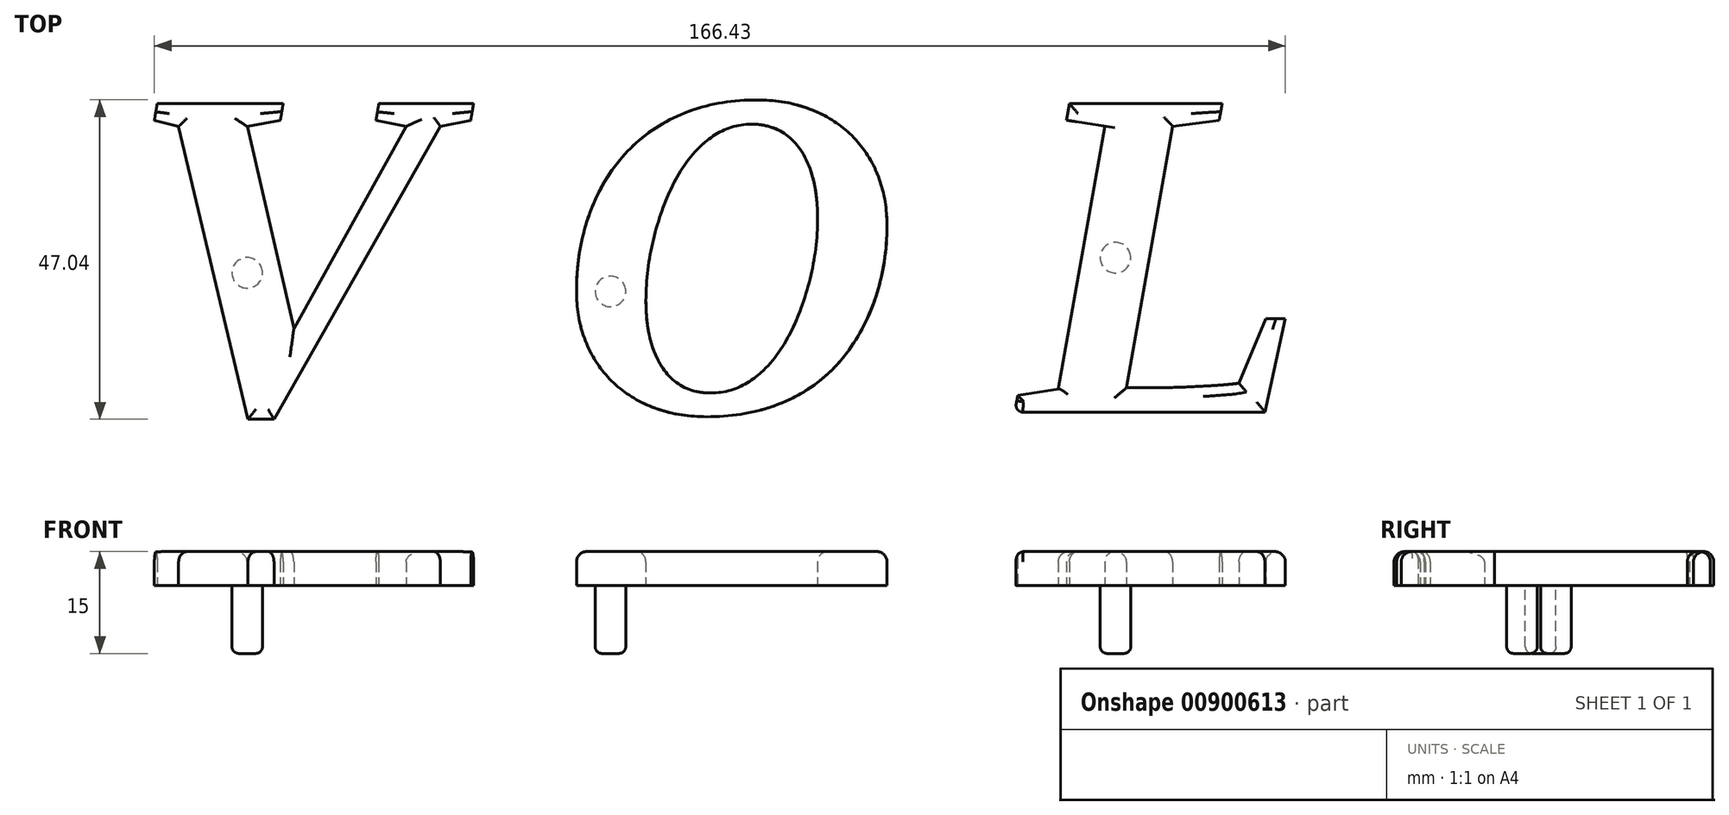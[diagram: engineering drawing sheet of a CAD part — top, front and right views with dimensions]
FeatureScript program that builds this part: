
annotation { "Feature Type Name" : "Feature", "Feature Type Description" : "" }
export const myFeature = defineFeature(function(context is Context, id is Id, definition is map)
    precondition{}
    {
        {
            var Q0;
            Q0=qCreatedBy(makeId("Top.planeOp"),FACE);
            var sketch = newSketch(context, id + "F0", { "sketchPlane" : qUnion([Q0])});
            skText(sketch, "E0", { "text": "V O L V O\n", "fontName": "Tinos-BoldItalic.ttf"});
            skPoint(sketch, "E1", {"position": v(51.81, -31.4) * mm});
            skPoint(sketch, "E2", {"position": v(27.28, -4.45) * mm});
            const initialGuessF0  = {"E0": [-0.05026, -0.04222, 1, 0, 0.05]};
            skSetInitialGuess(sketch, initialGuessF0);
            skSolve(sketch);
        }
        {
            var Q0;
            Q0 = qSketchRegion(id + "F0", true);
            extrude(context, id + "F1", {"entities" : qUnion([Q0]), "depth" : 5 * mm, "offsetDistance" : 25.4 * mm});
        }
        {
            var Q0;
            Q0=makeQuery(id+"F1.opExtrude","CAP_FACE",FACE,{"disambiguationData":[OSD([sQuery(id+"F0.wireOp",EDGE,"E0.sketch_text.stroke-0"),sQuery(id+"F0.wireOp",EDGE,"E0.sketch_text.stroke-1"),sQuery(id+"F0.wireOp",EDGE,"E0.sketch_text.stroke-2"),sQuery(id+"F0.wireOp",EDGE,"E0.sketch_text.stroke-3"),sQuery(id+"F0.wireOp",EDGE,"E0.sketch_text.stroke-4"),sQuery(id+"F0.wireOp",EDGE,"E0.sketch_text.stroke-5"),sQuery(id+"F0.wireOp",EDGE,"E0.sketch_text.stroke-6"),sQuery(id+"F0.wireOp",EDGE,"E0.sketch_text.stroke-7"),sQuery(id+"F0.wireOp",EDGE,"E0.sketch_text.stroke-8"),sQuery(id+"F0.wireOp",EDGE,"E0.sketch_text.stroke-9"),sQuery(id+"F0.wireOp",EDGE,"E0.sketch_text.stroke-10"),sQuery(id+"F0.wireOp",EDGE,"E0.sketch_text.stroke-11"),sQuery(id+"F0.wireOp",EDGE,"E0.sketch_text.stroke-12"),sQuery(id+"F0.wireOp",EDGE,"E0.sketch_text.stroke-13"),sQuery(id+"F0.wireOp",EDGE,"E0.sketch_text.stroke-14")])],"isStart":true});
            var sketch = newSketch(context, id + "F2", { "sketchPlane" : qUnion([Q0])});
            skPoint(sketch, "E3", {"position": v(-32.53, 21.7) * mm});
            skPoint(sketch, "E3.positionSnap0", {"position": v(-37.53, 21.7) * mm});
            skCircle(sketch, "E4", {"center": v(-32.53, 21.7) * mm, "radius": 2.25 * mm});
            skSolve(sketch);
        }
        {
            var Q0;
            Q0 = qSketchRegion(id + "F2", true);
            extrude(context, id + "F3", {"entities" : qUnion([Q0]), "operationType" : NewBodyOperationType.ADD, "depth" : 10 * mm, "offsetDistance" : 25 * mm});
        }
        {
            var Q0;
            Q0=makeQuery(id+"F1.opExtrude","CAP_FACE",FACE,{"disambiguationData":[OSD([sQuery(id+"F0.wireOp",EDGE,"E0.sketch_text.stroke-15"),sQuery(id+"F0.wireOp",EDGE,"E0.sketch_text.stroke-16"),sQuery(id+"F0.wireOp",EDGE,"E0.sketch_text.stroke-17"),sQuery(id+"F0.wireOp",EDGE,"E0.sketch_text.stroke-18"),sQuery(id+"F0.wireOp",EDGE,"E0.sketch_text.stroke-19"),sQuery(id+"F0.wireOp",EDGE,"E0.sketch_text.stroke-20"),sQuery(id+"F0.wireOp",EDGE,"E0.sketch_text.stroke-21"),sQuery(id+"F0.wireOp",EDGE,"E0.sketch_text.stroke-22"),sQuery(id+"F0.wireOp",EDGE,"E0.sketch_text.stroke-23"),sQuery(id+"F0.wireOp",EDGE,"E0.sketch_text.stroke-24"),sQuery(id+"F0.wireOp",EDGE,"E0.sketch_text.stroke-25"),sQuery(id+"F0.wireOp",EDGE,"E0.sketch_text.stroke-26"),sQuery(id+"F0.wireOp",EDGE,"E0.sketch_text.stroke-27"),sQuery(id+"F0.wireOp",EDGE,"E0.sketch_text.stroke-28"),sQuery(id+"F0.wireOp",EDGE,"E0.sketch_text.stroke-29"),sQuery(id+"F0.wireOp",EDGE,"E0.sketch_text.stroke-30"),sQuery(id+"F0.wireOp",EDGE,"E0.sketch_text.stroke-31"),sQuery(id+"F0.wireOp",EDGE,"E0.sketch_text.stroke-32"),sQuery(id+"F0.wireOp",EDGE,"E0.sketch_text.stroke-33"),sQuery(id+"F0.wireOp",EDGE,"E0.sketch_text.stroke-34"),sQuery(id+"F0.wireOp",EDGE,"E0.sketch_text.stroke-35"),sQuery(id+"F0.wireOp",EDGE,"E0.sketch_text.stroke-36")])],"isStart":true});
            var sketch = newSketch(context, id + "F4", { "sketchPlane" : qUnion([Q0])});
            skPoint(sketch, "E5", {"position": v(20.93, 24.45) * mm});
            skCircle(sketch, "E6", {"center": v(20.93, 24.45) * mm, "radius": 2.25 * mm});
            skSolve(sketch);
        }
        {
            var Q0;
            Q0 = qSketchRegion(id + "F4", true);
            extrude(context, id + "F5", {"entities" : qUnion([Q0]), "operationType" : NewBodyOperationType.ADD, "depth" : 10 * mm, "offsetDistance" : 25 * mm});
        }
        {
            var Q0;
            Q0=makeQuery(id+"F1.opExtrude","CAP_FACE",FACE,{"disambiguationData":[OSD([sQuery(id+"F0.wireOp",EDGE,"E0.sketch_text.stroke-37"),sQuery(id+"F0.wireOp",EDGE,"E0.sketch_text.stroke-38"),sQuery(id+"F0.wireOp",EDGE,"E0.sketch_text.stroke-39"),sQuery(id+"F0.wireOp",EDGE,"E0.sketch_text.stroke-40"),sQuery(id+"F0.wireOp",EDGE,"E0.sketch_text.stroke-41"),sQuery(id+"F0.wireOp",EDGE,"E0.sketch_text.stroke-42"),sQuery(id+"F0.wireOp",EDGE,"E0.sketch_text.stroke-43"),sQuery(id+"F0.wireOp",EDGE,"E0.sketch_text.stroke-44"),sQuery(id+"F0.wireOp",EDGE,"E0.sketch_text.stroke-45"),sQuery(id+"F0.wireOp",EDGE,"E0.sketch_text.stroke-46"),sQuery(id+"F0.wireOp",EDGE,"E0.sketch_text.stroke-47"),sQuery(id+"F0.wireOp",EDGE,"E0.sketch_text.stroke-48"),sQuery(id+"F0.wireOp",EDGE,"E0.sketch_text.stroke-49"),sQuery(id+"F0.wireOp",EDGE,"E0.sketch_text.stroke-50"),sQuery(id+"F0.wireOp",EDGE,"E0.sketch_text.stroke-51"),sQuery(id+"F0.wireOp",EDGE,"E0.sketch_text.stroke-52")])],"isStart":true});
            var sketch = newSketch(context, id + "F6", { "sketchPlane" : qUnion([Q0])});
            skPoint(sketch, "E7", {"position": v(95.24, 19.47) * mm});
            skPoint(sketch, "E7.positionSnap0", {"position": v(90.24, 19.47) * mm});
            skCircle(sketch, "E8", {"center": v(95.24, 19.47) * mm, "radius": 2.25 * mm});
            skSolve(sketch);
        }
        {
            var Q0;
            Q0 = qSketchRegion(id + "F6", true);
            extrude(context, id + "F7", {"entities" : qUnion([Q0]), "operationType" : NewBodyOperationType.ADD, "depth" : 10 * mm, "offsetDistance" : 25 * mm});
        }
        {
            var Q0;
            Q0=makeQuery(id+"F1.opExtrude","SWEPT_BODY",BODY,{"disambiguationData":[OSD([sQuery(id+"F0.wireOp",EDGE,"E0.sketch_text.stroke-53"),sQuery(id+"F0.wireOp",EDGE,"E0.sketch_text.stroke-54"),sQuery(id+"F0.wireOp",EDGE,"E0.sketch_text.stroke-55"),sQuery(id+"F0.wireOp",EDGE,"E0.sketch_text.stroke-56"),sQuery(id+"F0.wireOp",EDGE,"E0.sketch_text.stroke-57"),sQuery(id+"F0.wireOp",EDGE,"E0.sketch_text.stroke-58"),sQuery(id+"F0.wireOp",EDGE,"E0.sketch_text.stroke-59"),sQuery(id+"F0.wireOp",EDGE,"E0.sketch_text.stroke-60"),sQuery(id+"F0.wireOp",EDGE,"E0.sketch_text.stroke-61"),sQuery(id+"F0.wireOp",EDGE,"E0.sketch_text.stroke-62"),sQuery(id+"F0.wireOp",EDGE,"E0.sketch_text.stroke-63"),sQuery(id+"F0.wireOp",EDGE,"E0.sketch_text.stroke-64"),sQuery(id+"F0.wireOp",EDGE,"E0.sketch_text.stroke-65"),sQuery(id+"F0.wireOp",EDGE,"E0.sketch_text.stroke-66"),sQuery(id+"F0.wireOp",EDGE,"E0.sketch_text.stroke-67")])]});
            var Q1;
            Q1=makeQuery(id+"F1.opExtrude","SWEPT_BODY",BODY,{"disambiguationData":[OSD([sQuery(id+"F0.wireOp",EDGE,"E0.sketch_text.stroke-68"),sQuery(id+"F0.wireOp",EDGE,"E0.sketch_text.stroke-69"),sQuery(id+"F0.wireOp",EDGE,"E0.sketch_text.stroke-70"),sQuery(id+"F0.wireOp",EDGE,"E0.sketch_text.stroke-71"),sQuery(id+"F0.wireOp",EDGE,"E0.sketch_text.stroke-72"),sQuery(id+"F0.wireOp",EDGE,"E0.sketch_text.stroke-73"),sQuery(id+"F0.wireOp",EDGE,"E0.sketch_text.stroke-74"),sQuery(id+"F0.wireOp",EDGE,"E0.sketch_text.stroke-75"),sQuery(id+"F0.wireOp",EDGE,"E0.sketch_text.stroke-76"),sQuery(id+"F0.wireOp",EDGE,"E0.sketch_text.stroke-77"),sQuery(id+"F0.wireOp",EDGE,"E0.sketch_text.stroke-78"),sQuery(id+"F0.wireOp",EDGE,"E0.sketch_text.stroke-79"),sQuery(id+"F0.wireOp",EDGE,"E0.sketch_text.stroke-80"),sQuery(id+"F0.wireOp",EDGE,"E0.sketch_text.stroke-81"),sQuery(id+"F0.wireOp",EDGE,"E0.sketch_text.stroke-82"),sQuery(id+"F0.wireOp",EDGE,"E0.sketch_text.stroke-83"),sQuery(id+"F0.wireOp",EDGE,"E0.sketch_text.stroke-84"),sQuery(id+"F0.wireOp",EDGE,"E0.sketch_text.stroke-85"),sQuery(id+"F0.wireOp",EDGE,"E0.sketch_text.stroke-86"),sQuery(id+"F0.wireOp",EDGE,"E0.sketch_text.stroke-87"),sQuery(id+"F0.wireOp",EDGE,"E0.sketch_text.stroke-88"),sQuery(id+"F0.wireOp",EDGE,"E0.sketch_text.stroke-89")])]});
            deleteBodies(context, id + "F8", {"entities" : qUnion([Q0, Q1])});
        }
        {
            var Q0;
            Q0=makeQuery(id+"F1.opExtrude","CAP_FACE",FACE,{"disambiguationData":[OSD([sQuery(id+"F0.wireOp",EDGE,"E0.sketch_text.stroke-0"),sQuery(id+"F0.wireOp",EDGE,"E0.sketch_text.stroke-1"),sQuery(id+"F0.wireOp",EDGE,"E0.sketch_text.stroke-2"),sQuery(id+"F0.wireOp",EDGE,"E0.sketch_text.stroke-3"),sQuery(id+"F0.wireOp",EDGE,"E0.sketch_text.stroke-4"),sQuery(id+"F0.wireOp",EDGE,"E0.sketch_text.stroke-5"),sQuery(id+"F0.wireOp",EDGE,"E0.sketch_text.stroke-6"),sQuery(id+"F0.wireOp",EDGE,"E0.sketch_text.stroke-7"),sQuery(id+"F0.wireOp",EDGE,"E0.sketch_text.stroke-8"),sQuery(id+"F0.wireOp",EDGE,"E0.sketch_text.stroke-9"),sQuery(id+"F0.wireOp",EDGE,"E0.sketch_text.stroke-10"),sQuery(id+"F0.wireOp",EDGE,"E0.sketch_text.stroke-11"),sQuery(id+"F0.wireOp",EDGE,"E0.sketch_text.stroke-12"),sQuery(id+"F0.wireOp",EDGE,"E0.sketch_text.stroke-13"),sQuery(id+"F0.wireOp",EDGE,"E0.sketch_text.stroke-14")])],"isStart":false});
            var Q1;
            Q1=makeQuery(id+"F1.opExtrude","CAP_FACE",FACE,{"disambiguationData":[OSD([sQuery(id+"F0.wireOp",EDGE,"E0.sketch_text.stroke-15"),sQuery(id+"F0.wireOp",EDGE,"E0.sketch_text.stroke-16"),sQuery(id+"F0.wireOp",EDGE,"E0.sketch_text.stroke-17"),sQuery(id+"F0.wireOp",EDGE,"E0.sketch_text.stroke-18"),sQuery(id+"F0.wireOp",EDGE,"E0.sketch_text.stroke-19"),sQuery(id+"F0.wireOp",EDGE,"E0.sketch_text.stroke-20"),sQuery(id+"F0.wireOp",EDGE,"E0.sketch_text.stroke-21"),sQuery(id+"F0.wireOp",EDGE,"E0.sketch_text.stroke-22"),sQuery(id+"F0.wireOp",EDGE,"E0.sketch_text.stroke-23"),sQuery(id+"F0.wireOp",EDGE,"E0.sketch_text.stroke-24"),sQuery(id+"F0.wireOp",EDGE,"E0.sketch_text.stroke-25"),sQuery(id+"F0.wireOp",EDGE,"E0.sketch_text.stroke-26"),sQuery(id+"F0.wireOp",EDGE,"E0.sketch_text.stroke-27"),sQuery(id+"F0.wireOp",EDGE,"E0.sketch_text.stroke-28"),sQuery(id+"F0.wireOp",EDGE,"E0.sketch_text.stroke-29"),sQuery(id+"F0.wireOp",EDGE,"E0.sketch_text.stroke-30"),sQuery(id+"F0.wireOp",EDGE,"E0.sketch_text.stroke-31"),sQuery(id+"F0.wireOp",EDGE,"E0.sketch_text.stroke-32"),sQuery(id+"F0.wireOp",EDGE,"E0.sketch_text.stroke-33"),sQuery(id+"F0.wireOp",EDGE,"E0.sketch_text.stroke-34"),sQuery(id+"F0.wireOp",EDGE,"E0.sketch_text.stroke-35"),sQuery(id+"F0.wireOp",EDGE,"E0.sketch_text.stroke-36")])],"isStart":false});
            var Q2;
            Q2=makeQuery(id+"F1.opExtrude","CAP_EDGE",EDGE,{"disambiguationData":[OSD([sQuery(id+"F0.wireOp",EDGE,"E0.sketch_text.stroke-49")])],"isStart":false});
            var Q3;
            Q3=makeQuery(id+"F1.opExtrude","CAP_EDGE",EDGE,{"disambiguationData":[OSD([sQuery(id+"F0.wireOp",EDGE,"E0.sketch_text.stroke-48")])],"isStart":false});
            var Q4;
            Q4=makeQuery(id+"F1.opExtrude","CAP_EDGE",EDGE,{"disambiguationData":[OSD([sQuery(id+"F0.wireOp",EDGE,"E0.sketch_text.stroke-46")])],"isStart":false});
            var Q5;
            Q5=makeQuery(id+"F1.opExtrude","CAP_EDGE",EDGE,{"disambiguationData":[OSD([sQuery(id+"F0.wireOp",EDGE,"E0.sketch_text.stroke-52")])],"isStart":false});
            var Q6;
            Q6=makeQuery(id+"F1.opExtrude","CAP_EDGE",EDGE,{"disambiguationData":[OSD([sQuery(id+"F0.wireOp",EDGE,"E0.sketch_text.stroke-51")])],"isStart":false});
            var Q7;
            Q7=makeQuery(id+"F1.opExtrude","CAP_EDGE",EDGE,{"disambiguationData":[OSD([sQuery(id+"F0.wireOp",EDGE,"E0.sketch_text.stroke-50")])],"isStart":false});
            var Q8;
            Q8=makeQuery(id+"F1.opExtrude","CAP_EDGE",EDGE,{"disambiguationData":[OSD([sQuery(id+"F0.wireOp",EDGE,"E0.sketch_text.stroke-37")])],"isStart":false});
            var Q9;
            Q9=makeQuery(id+"F1.opExtrude","CAP_EDGE",EDGE,{"disambiguationData":[OSD([sQuery(id+"F0.wireOp",EDGE,"E0.sketch_text.stroke-38")])],"isStart":false});
            var Q10;
            Q10=makeQuery(id+"F1.opExtrude","CAP_EDGE",EDGE,{"disambiguationData":[OSD([sQuery(id+"F0.wireOp",EDGE,"E0.sketch_text.stroke-40")])],"isStart":false});
            var Q11;
            Q11=makeQuery(id+"F1.opExtrude","CAP_EDGE",EDGE,{"disambiguationData":[OSD([sQuery(id+"F0.wireOp",EDGE,"E0.sketch_text.stroke-41")])],"isStart":false});
            var Q12;
            Q12=makeQuery(id+"F1.opExtrude","CAP_EDGE",EDGE,{"disambiguationData":[OSD([sQuery(id+"F0.wireOp",EDGE,"E0.sketch_text.stroke-42")])],"isStart":false});
            var Q13;
            Q13=makeQuery(id+"F1.opExtrude","CAP_EDGE",EDGE,{"disambiguationData":[OSD([sQuery(id+"F0.wireOp",EDGE,"E0.sketch_text.stroke-43")])],"isStart":false});
            fillet(context, id + "F9", {"entities" : qUnion([Q0, Q1, Q2, Q3, Q4, Q5, Q6, Q7, Q8, Q9, Q10, Q11, Q12, Q13]), "radius" : 1.5 * mm, "tangentPropagation" : true, "allowEdgeOverflow" : false});
        }
        {
            var Q0;
            Q0=makeQuery(id+"F1.opExtrude","CAP_EDGE",EDGE,{"disambiguationData":[OSD([sQuery(id+"F0.wireOp",EDGE,"E0.sketch_text.stroke-44")])],"isStart":false});
            var Q1;
            Q1=makeQuery(id+"F1.opExtrude","CAP_EDGE",EDGE,{"disambiguationData":[OSD([sQuery(id+"F0.wireOp",EDGE,"E0.sketch_text.stroke-45")])],"isStart":false});
            fillet(context, id + "F10", {"entities" : qUnion([Q0, Q1]), "radius" : 1 * mm, "tangentPropagation" : true, "allowEdgeOverflow" : false});
        }
        {
            var Q0;
            Q0=makeQuery(id+"F7.opExtrude","CAP_EDGE",EDGE,{"disambiguationData":[OSD([sQuery(id+"F6.wireOp",EDGE,"E8")])],"isStart":false});
            var Q1;
            Q1=makeQuery(id+"F5.opExtrude","CAP_EDGE",EDGE,{"disambiguationData":[OSD([sQuery(id+"F4.wireOp",EDGE,"E6")])],"isStart":false});
            var Q2;
            Q2=makeQuery(id+"F3.opExtrude","CAP_EDGE",EDGE,{"disambiguationData":[OSD([sQuery(id+"F2.wireOp",EDGE,"E4")])],"isStart":false});
            fillet(context, id + "F11", {"entities" : qUnion([Q0, Q1, Q2]), "radius" : 1 * mm, "tangentPropagation" : true, "allowEdgeOverflow" : false});
        }
    });
